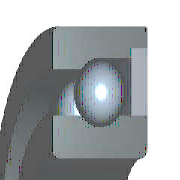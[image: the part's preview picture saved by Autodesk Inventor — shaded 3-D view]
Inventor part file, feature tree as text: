
AUTODESK INVENTOR PART (.ipt)
format: ipt  version: 2015 (Build 190159000, 159)  size: 306,176 bytes
history: native  units: mm (DEFAULTED — no unit token found)
features: sketch x1, other x1, pattern_circular x1
ambient origin geometry x8: Origin, YZ Plane, XZ Plane, XY Plane, X Axis, Y Axis, Z Axis, Center Point
bodies: Body (feature_tree)
feature tree (3):
  sketch  "Sketch"  dims[d0=2.86mm d55=90.0deg d1=0.3mm d2=0.1mm d58=90.0deg d3=70.0mm d4=360.0deg d5=0.0mm d6=0.0mm d7=0.0mm d8=8.0mm d9=13.5mm d10=19.0mm d11=17.178mm d12=11.586mm d13=6.0mm d14=6.0mm d15=5.0mm d16=3.0mm d17=0.0mm d18=0.0mm]
  other  "Ball"
  pattern_circular  "Balls"  Angle=90.0deg  [1 undecoded]
note: 1 required parameter value undecoded (feature->parameter linkage not recoverable at this tier; creation-order binding heuristic only, values carry confidence <= 0.55)
